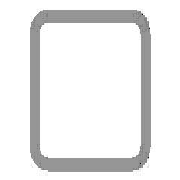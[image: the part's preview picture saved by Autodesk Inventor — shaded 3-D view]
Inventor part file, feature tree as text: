
AUTODESK INVENTOR PART (.ipt)
format: ipt  version: 2022 (Build 260153000, 153)  size: 147,968 bytes
history: native  units: mm (DEFAULTED — no unit token found)
features: other x4, sketch x3, plane x2, extrude x1, split x1
ambient origin geometry x8: Origin, YZ Plane, XZ Plane, XY Plane, X Axis, Y Axis, Z Axis, Center Point
bodies: Solid1 (feature_tree)
feature tree (11):
  parser-record x1  (decoder bookkeeping rows leaked as tree rows — omitted from the tree; the rows remain in map.json)
  other  "Driven Length"
  other  "Plano inicial"
  other  "Plano final"
  extrude  "Cuerpo"  TaperAngle=0.0deg  [1 undecoded]
  plane  "Plano de trabajo4"
  split  "Dividir1"
  sketch  "Boceto"  dims[d10=40.0mm d11=40.0mm d12=5.0mm d13=-11.768067mm d14=330.0mm d15=20.0mm d16=20.0mm d17=90.0deg d18=341.768067mm]
  sketch  "Sketch3"  dims[d3=341.768067mm d4=0.0mm]
  plane  "Work Plane3"
  sketch  "Sketch4"  dims[d7=7.5mm]
note: 1 required parameter value undecoded (feature->parameter linkage not recoverable at this tier; creation-order binding heuristic only, values carry confidence <= 0.55)
